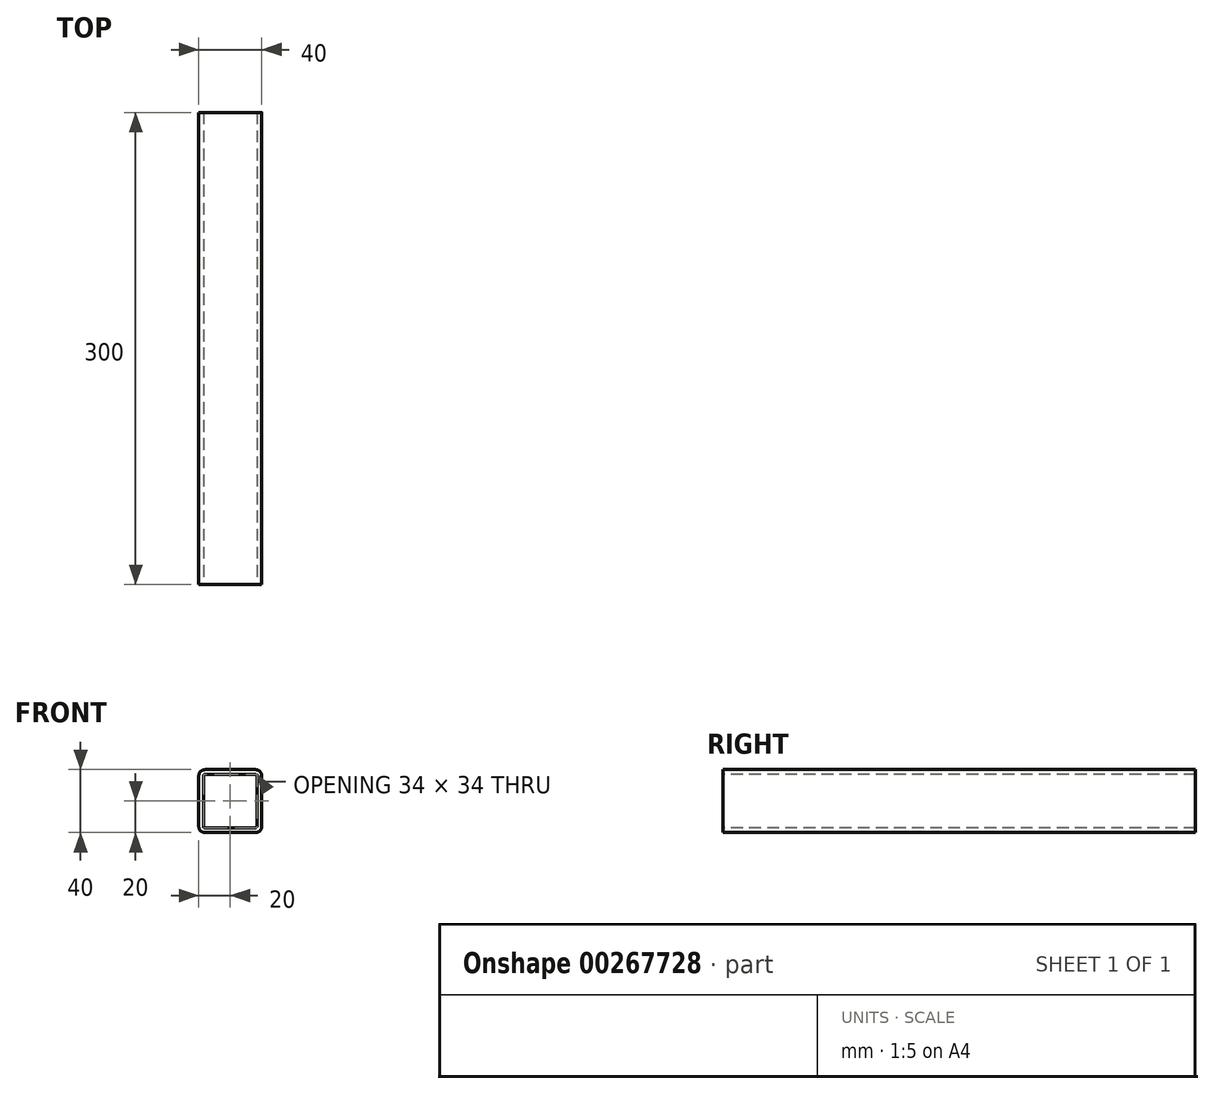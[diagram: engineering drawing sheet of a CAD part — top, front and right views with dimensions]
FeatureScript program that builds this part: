
annotation { "Feature Type Name" : "Feature", "Feature Type Description" : "" }
export const myFeature = defineFeature(function(context is Context, id is Id, definition is map)
    precondition{}
    {
        {
            var Q0;
            Q0=qCreatedBy(makeId("Front.planeOp"),FACE);
            var sketch = newSketch(context, id + "F0", { "sketchPlane" : qUnion([Q0])});
            skLineSegment(sketch, "E0.bottom", {"start": v(16, -20) * mm, "end": v(-16, -20) * mm});
            skLineSegment(sketch, "E0.top", {"start": v(16, 20) * mm, "end": v(-16, 20) * mm});
            skLineSegment(sketch, "E0.left", {"start": v(20, -16) * mm, "end": v(20, 16) * mm});
            skLineSegment(sketch, "E0.right", {"start": v(-20, -16) * mm, "end": v(-20, 16) * mm});
            skPoint(sketch, "E0.middle", {"position": v(0, 0) * mm});
            skPoint(sketch, "E1.visualSharp", {"position": v(-20, 20) * mm});
            skArc(sketch, "E1.filletArc", {"start": v(-16, 20) * mm, "mid": v(-18.83, 18.83) * mm, "end": v(-20, 16) * mm});
            skPoint(sketch, "E2.visualSharp", {"position": v(20, 20) * mm});
            skArc(sketch, "E2.filletArc", {"start": v(20, 16) * mm, "mid": v(18.83, 18.83) * mm, "end": v(16, 20) * mm});
            skPoint(sketch, "E3.visualSharp", {"position": v(20, -20) * mm});
            skArc(sketch, "E3.filletArc", {"start": v(16, -20) * mm, "mid": v(18.83, -18.83) * mm, "end": v(20, -16) * mm});
            skPoint(sketch, "E4.visualSharp", {"position": v(-20, -20) * mm});
            skArc(sketch, "E4.filletArc", {"start": v(-20, -16) * mm, "mid": v(-18.83, -18.83) * mm, "end": v(-16, -20) * mm});
            skArc(sketch, "E5.0", {"start": v(-17, -16) * mm, "mid": v(-16.7, -16.7) * mm, "end": v(-16, -17) * mm});
            skLineSegment(sketch, "E5.1", {"start": v(16, -17) * mm, "end": v(-16, -17) * mm});
            skLineSegment(sketch, "E5.2", {"start": v(-17, -16) * mm, "end": v(-17, 16) * mm});
            skArc(sketch, "E5.3", {"start": v(16, -17) * mm, "mid": v(16.7, -16.7) * mm, "end": v(17, -16) * mm});
            skArc(sketch, "E5.4", {"start": v(-16, 17) * mm, "mid": v(-16.7, 16.7) * mm, "end": v(-17, 16) * mm});
            skLineSegment(sketch, "E5.5", {"start": v(16, 17) * mm, "end": v(-16, 17) * mm});
            skArc(sketch, "E5.6", {"start": v(17, 16) * mm, "mid": v(16.7, 16.7) * mm, "end": v(16, 17) * mm});
            skLineSegment(sketch, "E5.7", {"start": v(17, -16) * mm, "end": v(17, 16) * mm});
            skSolve(sketch);
        }
        {
            var Q0;
            Q0=qSketchRegion(id+"F0",true);
            extrude(context, id + "F1", {"entities" : qUnion([Q0]), "oppositeDirection" : true, "depth" : 300 * mm});
        }
    });
